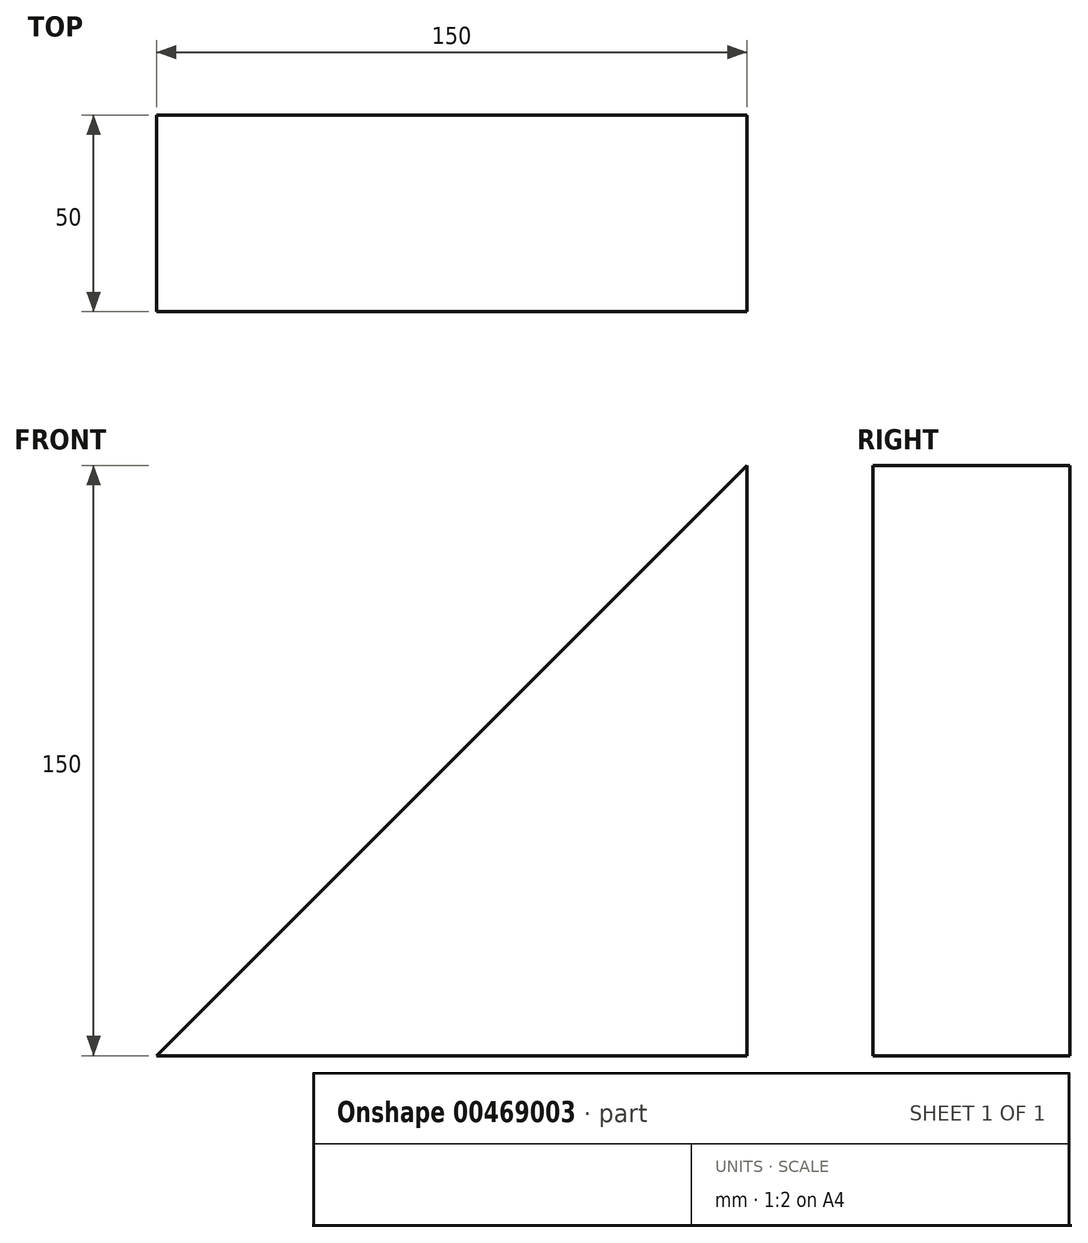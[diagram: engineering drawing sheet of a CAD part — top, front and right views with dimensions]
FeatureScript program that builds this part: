
annotation { "Feature Type Name" : "Feature", "Feature Type Description" : "" }
export const myFeature = defineFeature(function(context is Context, id is Id, definition is map)
    precondition{}
    {
        {
            var Q0;
            Q0=qCreatedBy(makeId("Front.planeOp"),FACE);
            var sketch = newSketch(context, id + "F0", { "sketchPlane" : qUnion([Q0])});
            skLineSegment(sketch, "E0", {"start": v(0, 0) * mm, "end": v(150, 0) * mm});
            skLineSegment(sketch, "E1", {"start": v(150, 0) * mm, "end": v(150, 150) * mm});
            skLineSegment(sketch, "E2", {"start": v(0, 0) * mm, "end": v(150, 150) * mm});
            skSolve(sketch);
        }
        {
            var Q0;
            Q0=makeQuery(id+"F0.imprint","IMPRINT",FACE,{"disambiguationData":[TD([[makeQuery(id+"F0.imprint","IMPRINT",EDGE,{"derivedFrom":sQuery(id+"F0.wireOp",EDGE,"E0")}),1.0]])]});
            extrude(context, id + "F1", {"entities" : qUnion([Q0]), "depth" : 50 * mm});
        }
    });
